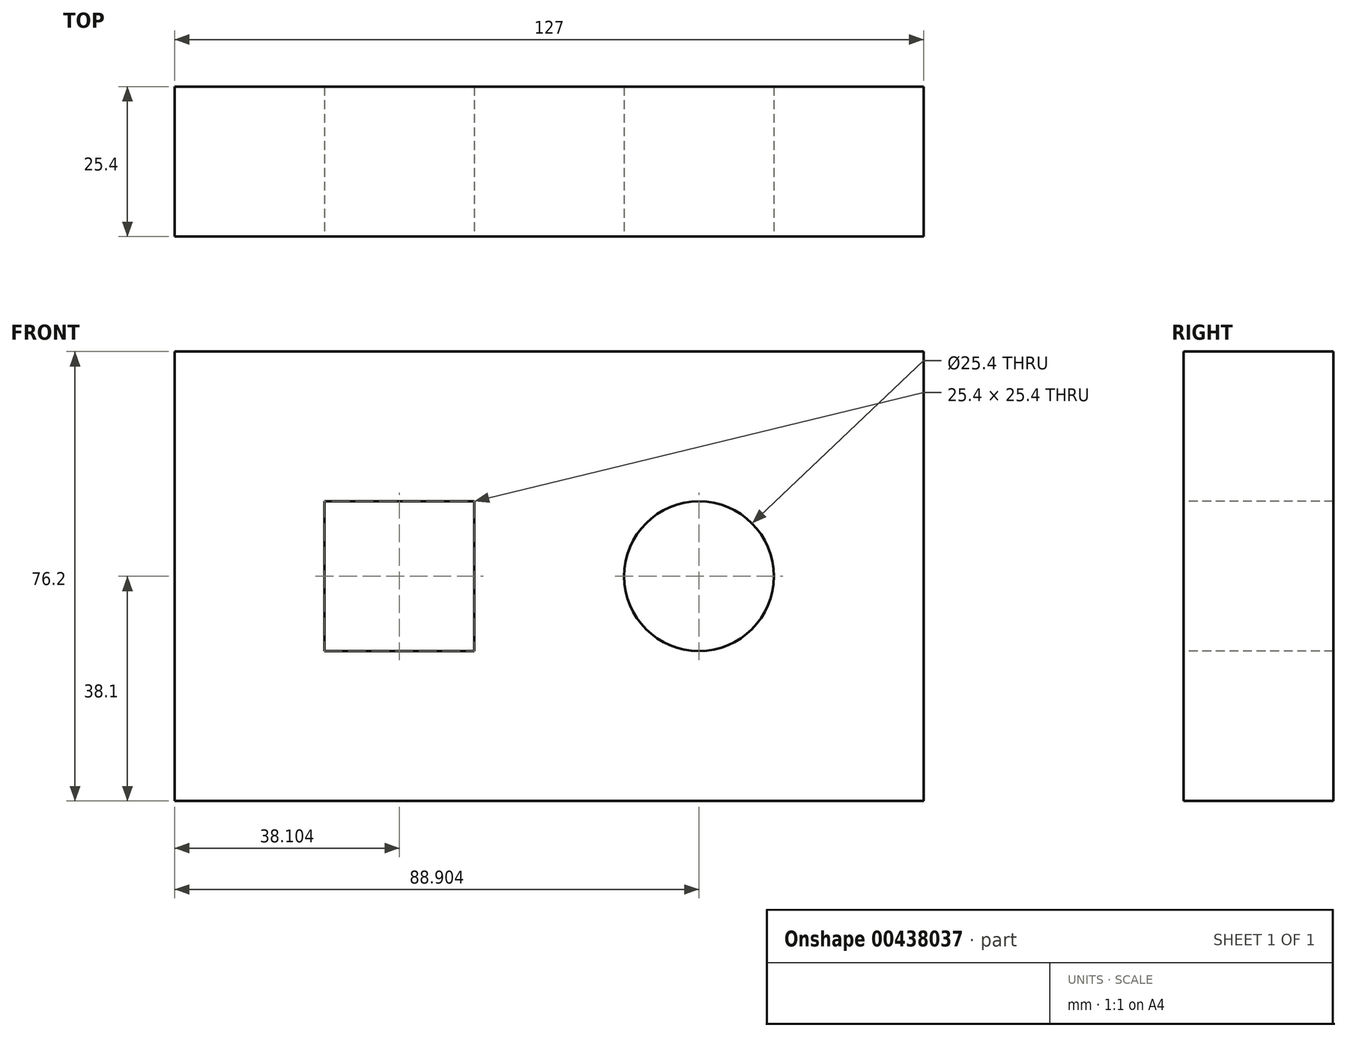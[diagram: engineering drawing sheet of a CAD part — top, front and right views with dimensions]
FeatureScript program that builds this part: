
annotation { "Feature Type Name" : "Feature", "Feature Type Description" : "" }
export const myFeature = defineFeature(function(context is Context, id is Id, definition is map)
    precondition{}
    {
        {
            var Q0;
            Q0=qCreatedBy(makeId("Front.planeOp"),FACE);
            var sketch = newSketch(context, id + "F0", { "sketchPlane" : qUnion([Q0])});
            skLineSegment(sketch, "E0.bottom", {"start": v(50.8, 0) * mm, "end": v(-76.2, 0) * mm});
            skLineSegment(sketch, "E0.top", {"start": v(50.8, 76.2) * mm, "end": v(-76.2, 76.2) * mm});
            skLineSegment(sketch, "E0.left", {"start": v(50.8, 0) * mm, "end": v(50.8, 76.2) * mm});
            skLineSegment(sketch, "E0.right", {"start": v(-76.2, 0) * mm, "end": v(-76.2, 76.2) * mm});
            skSolve(sketch);
        }
        {
            var Q0;
            Q0=makeQuery(id+"F0.imprint","IMPRINT",FACE,{"disambiguationData":[TD([[makeQuery(id+"F0.imprint","IMPRINT",EDGE,{"derivedFrom":sQuery(id+"F0.wireOp",EDGE,"E0.bottom")}),-1.0]])]});
            extrude(context, id + "F1", {"entities" : qUnion([Q0]), "depth" : 25.4 * mm});
        }
        {
            var Q0;
            Q0=makeQuery(id+"F1.opExtrude","CAP_FACE",FACE,{"disambiguationData":[OSD([sQuery(id+"F0.wireOp",EDGE,"E0.bottom"),sQuery(id+"F0.wireOp",EDGE,"E0.top"),sQuery(id+"F0.wireOp",EDGE,"E0.left"),sQuery(id+"F0.wireOp",EDGE,"E0.right")])],"isStart":false});
            var sketch = newSketch(context, id + "F2", { "sketchPlane" : qUnion([Q0])});
            skLineSegment(sketch, "E1.bottom", {"start": v(-50.8, 25.4) * mm, "end": v(-25.4, 25.4) * mm});
            skLineSegment(sketch, "E1.top", {"start": v(-25.4, 50.8) * mm, "end": v(-50.8, 50.8) * mm});
            skLineSegment(sketch, "E1.left", {"start": v(-25.4, 50.8) * mm, "end": v(-25.4, 25.4) * mm});
            skLineSegment(sketch, "E1.right", {"start": v(-50.8, 50.8) * mm, "end": v(-50.8, 25.4) * mm});
            skSolve(sketch);
        }
        {
            var Q0;
            Q0=makeQuery(id+"F2.imprint","IMPRINT",FACE,{"disambiguationData":[TD([[makeQuery(id+"F2.imprint","IMPRINT",EDGE,{"derivedFrom":sQuery(id+"F2.wireOp",EDGE,"E1.bottom")}),-1.0]])]});
            var sketch = newSketch(context, id + "F3", { "sketchPlane" : qUnion([Q0])});
            skCircle(sketch, "E2", {"center": v(12.7, 38.1) * mm, "radius": 12.7 * mm});
            skSolve(sketch);
        }
        {
            var Q0;
            Q0=makeQuery(id+"F2.imprint","IMPRINT",FACE,{"disambiguationData":[TD([[makeQuery(id+"F2.imprint","IMPRINT",EDGE,{"derivedFrom":sQuery(id+"F2.wireOp",EDGE,"E1.bottom")}),1.0]])]});
            extrude(context, id + "F4", {"entities" : qUnion([Q0]), "operationType" : NewBodyOperationType.REMOVE, "oppositeDirection" : true, "depth" : 50.8 * mm});
        }
        {
            var Q0;
            Q0 = qSketchRegion(id + "F3", true);
            extrude(context, id + "F5", {"entities" : qUnion([Q0]), "operationType" : NewBodyOperationType.REMOVE, "oppositeDirection" : true, "depth" : 50.8 * mm});
        }
    });
